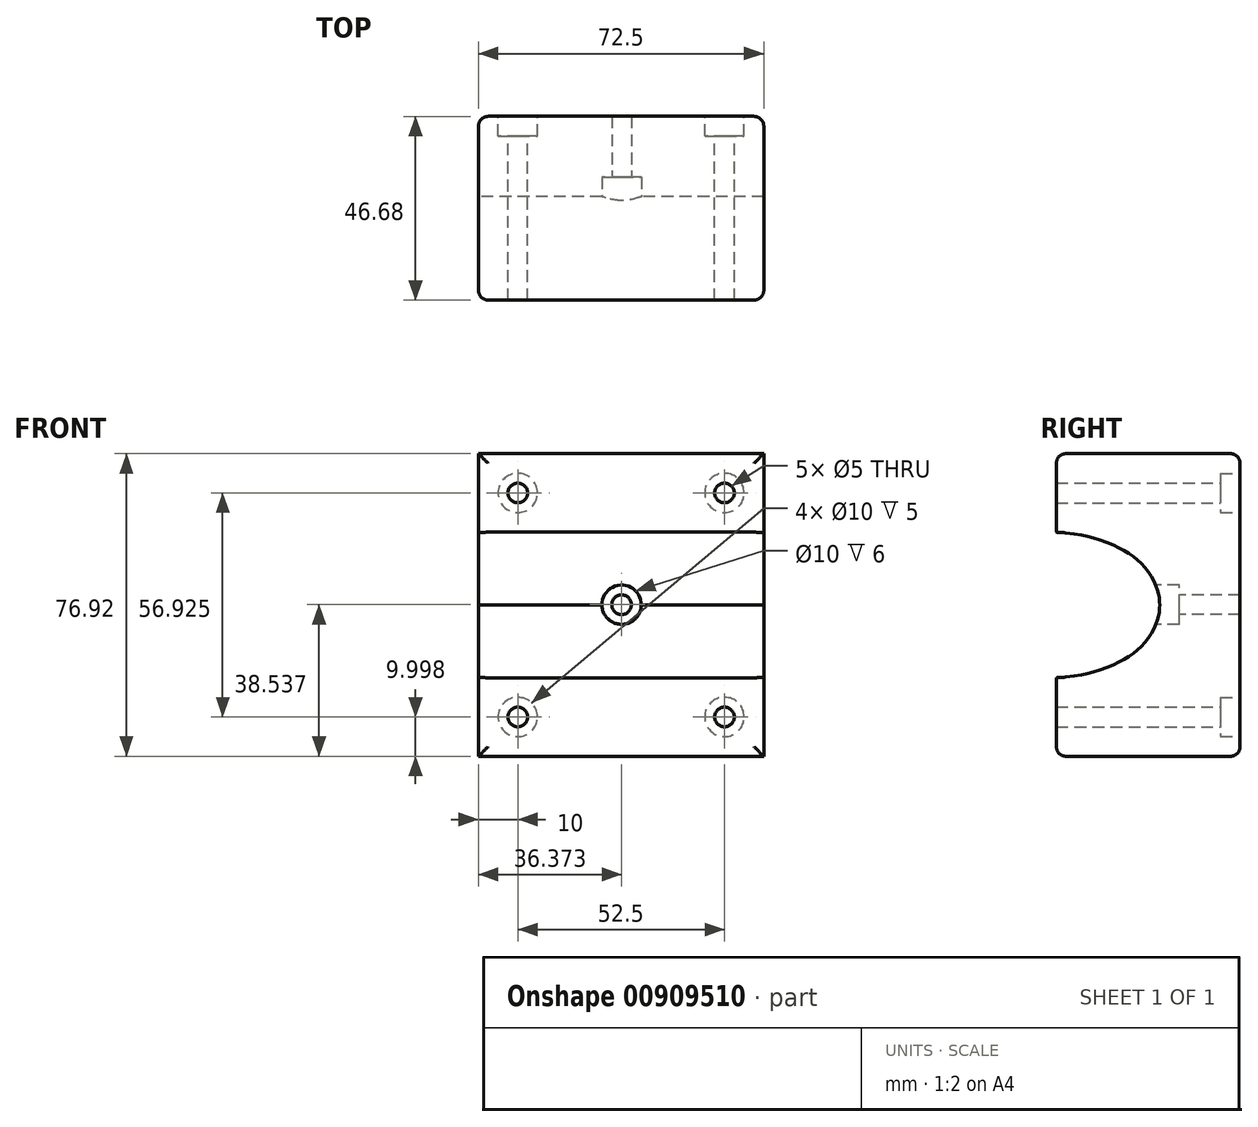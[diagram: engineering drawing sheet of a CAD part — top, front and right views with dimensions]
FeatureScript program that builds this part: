
annotation { "Feature Type Name" : "Feature", "Feature Type Description" : "" }
export const myFeature = defineFeature(function(context is Context, id is Id, definition is map)
    precondition{}
    {
        {
            var Q0;
            Q0=qCreatedBy(makeId("Right.planeOp"),FACE);
            var sketch = newSketch(context, id + "F0", { "sketchPlane" : qUnion([Q0])});
            skFitSpline(sketch, "E0.0", {"points": [v(-65.87, 0.89) * mm, v(-64.8, 1.67) * mm, v(-62.45, 3.19) * mm, v(-57.02, 6.06) * mm, v(-50.73, 8.67) * mm, v(-44.06, 10.98) * mm, v(-38.98, 12.54) * mm, v(-33.97, 13.9) * mm, v(-27.45, 15.46) * mm, v(-21.18, 16.65) * mm, v(-15.26, 17.5) * mm, v(-11.02, 18) * mm, v(-7, 18.34) * mm, v(-3.2, 18.55) * mm, v(0.4, 18.66) * mm, v(3.25, 18.68) * mm, v(5.47, 18.65) * mm, v(7.1, 18.62) * mm, v(8.7, 18.58) * mm, v(10.8, 18.5) * mm, v(13.41, 18.32) * mm, v(15.98, 18.01) * mm, v(18.01, 17.64) * mm, v(19.53, 17.3) * mm, v(21.04, 16.88) * mm, v(22.99, 16.25) * mm, v(24.85, 15.51) * mm, v(26.59, 14.7) * mm, v(27.81, 14.07) * mm, v(28.95, 13.42) * mm, v(30, 12.76) * mm, v(30.96, 12.06) * mm, v(31.85, 11.32) * mm, v(32.68, 10.52) * mm, v(33.46, 9.67) * mm, v(34.18, 8.74) * mm, v(34.86, 7.74) * mm, v(35.5, 6.7) * mm, v(36.05, 5.65) * mm, v(36.44, 4.76) * mm, v(36.7, 4.05) * mm, v(36.88, 3.52) * mm, v(37.01, 3) * mm, v(37.15, 2.32) * mm, v(37.25, 1.54) * mm, v(37.3, 0.7) * mm, v(37.3, 0.22) * mm, v(37.3, 0) * mm]});
            skLineSegment(sketch, "E1", {"start": v(11.06, 18.47) * mm, "end": v(11.06, 38.46) * mm});
            skLineSegment(sketch, "E2", {"start": v(11.06, 38.46) * mm, "end": v(57.74, 38.46) * mm});
            skFitSpline(sketch, "E3.MirrorCS", {"points": [v(-65.87, -0.89) * mm, v(-64.8, -1.67) * mm, v(-62.45, -3.19) * mm, v(-57.02, -6.06) * mm, v(-50.73, -8.67) * mm, v(-44.06, -10.98) * mm, v(-38.98, -12.54) * mm, v(-33.97, -13.9) * mm, v(-27.45, -15.46) * mm, v(-21.18, -16.65) * mm, v(-15.26, -17.5) * mm, v(-11.02, -18) * mm, v(-7, -18.34) * mm, v(-3.2, -18.55) * mm, v(0.4, -18.66) * mm, v(3.25, -18.68) * mm, v(5.47, -18.65) * mm, v(7.1, -18.62) * mm, v(8.7, -18.58) * mm, v(10.8, -18.5) * mm, v(13.41, -18.32) * mm, v(15.98, -18.01) * mm, v(18.01, -17.64) * mm, v(19.53, -17.3) * mm, v(21.04, -16.88) * mm, v(22.99, -16.25) * mm, v(24.85, -15.51) * mm, v(26.59, -14.7) * mm, v(27.81, -14.07) * mm, v(28.95, -13.42) * mm, v(30, -12.76) * mm, v(30.96, -12.06) * mm, v(31.85, -11.32) * mm, v(32.68, -10.52) * mm, v(33.46, -9.67) * mm, v(34.18, -8.74) * mm, v(34.86, -7.74) * mm, v(35.5, -6.7) * mm, v(36.05, -5.65) * mm, v(36.44, -4.76) * mm, v(36.7, -4.05) * mm, v(36.88, -3.52) * mm, v(37.01, -3) * mm, v(37.15, -2.32) * mm, v(37.25, -1.54) * mm, v(37.3, -0.7) * mm, v(37.3, -0.22) * mm, v(37.3, 0) * mm]});
            skLineSegment(sketch, "E4.MirrorCS", {"start": v(11.06, -38.46) * mm, "end": v(57.74, -38.46) * mm});
            skLineSegment(sketch, "E5.MirrorCS", {"start": v(11.06, -18.47) * mm, "end": v(11.06, -38.46) * mm});
            skLineSegment(sketch, "E6", {"start": v(57.74, 38.46) * mm, "end": v(57.74, -38.46) * mm});
            skSolve(sketch);
        }
        {
            var Q0;
            Q0=qSketchRegion(id+"F0",true);
            extrude(context, id + "F1", {"entities" : qUnion([Q0]), "depth" : 72.5 * mm, "offsetDistance" : 25 * mm});
        }
        {
            var Q0;
            Q0=makeQuery(id+"F1.opExtrude","SWEPT_FACE",FACE,{"disambiguationData":[OSD([sQuery(id+"F0.wireOp",EDGE,"E1")])]});
            var sketch = newSketch(context, id + "F2", { "sketchPlane" : qUnion([Q0])});
            skPoint(sketch, "E7", {"position": v(36.37, 0.08) * mm});
            skSolve(sketch);
        }
        {
            var Q0;
            Q0=sQuery(id+"F2.wireOp",VERTEX,"8a5668b4-76ee-41ec-8645-79288d4d8dce");
            var Q1;
            Q1=sQuery(id+"F2.wireOp",VERTEX,"E7");
            var Q2;
            Q2=makeQuery(id+"F1.opExtrude","SWEPT_BODY",BODY,{"disambiguationData":[OSD([sQuery(id+"F0.wireOp",EDGE,"E0.0"),sQuery(id+"F0.wireOp",EDGE,"E1"),sQuery(id+"F0.wireOp",EDGE,"E2"),sQuery(id+"F0.wireOp",EDGE,"E3.MirrorCS"),sQuery(id+"F0.wireOp",EDGE,"E4.MirrorCS"),sQuery(id+"F0.wireOp",EDGE,"E5.MirrorCS"),sQuery(id+"F0.wireOp",EDGE,"E6")])]});
            hole(context, id + "F3", {"style" : HoleStyle.C_BORE, "endStyle" : HoleEndStyle.THROUGH, "holeDiameter" : 5 * mm, "cBoreDiameter" : 10 * mm, "cBoreDepth" : 5 * mm, "majorDiameter" : 5 * mm, "isTappedThrough" : true, "tappedDepth" : 12 * mm, "tapClearance" : 3, "locations" : qUnion([Q0, Q1]), "scope" : qUnion([Q2])});
        }
        {
            var Q0;
            Q0=makeQuery(id+"F1.opExtrude","SWEPT_FACE",FACE,{"disambiguationData":[OSD([sQuery(id+"F0.wireOp",EDGE,"E6")])]});
            var sketch = newSketch(context, id + "F4", { "sketchPlane" : qUnion([Q0])});
            skSolve(sketch);
        }
        {
            var Q0;
            Q0=makeQuery(id+"F1.opExtrude","SWEPT_EDGE",EDGE,{"disambiguationData":[OSD([sQuery(id+"F0.wireOp",EDGE,"E4.MirrorCS"),sQuery(id+"F0.wireOp",EDGE,"E6")])]});
            var Q1;
            Q1=makeQuery(id+"F1.opExtrude","CAP_EDGE",EDGE,{"disambiguationData":[OSD([sQuery(id+"F0.wireOp",EDGE,"E6")])],"isStart":false});
            var Q2;
            Q2=makeQuery(id+"F1.opExtrude","SWEPT_EDGE",EDGE,{"disambiguationData":[OSD([sQuery(id+"F0.wireOp",EDGE,"E2"),sQuery(id+"F0.wireOp",EDGE,"E6")])]});
            var Q3;
            Q3=makeQuery(id+"F1.opExtrude","CAP_EDGE",EDGE,{"disambiguationData":[OSD([sQuery(id+"F0.wireOp",EDGE,"E6")])],"isStart":true});
            fillet(context, id + "F5", {"entities" : qUnion([Q0, Q1, Q2, Q3]), "radius" : 2.5 * mm, "tangentPropagation" : true, "allowEdgeOverflow" : false});
        }
        {
            var Q0;
            Q0=makeQuery(id+"F1.opExtrude","CAP_EDGE",EDGE,{"disambiguationData":[OSD([sQuery(id+"F0.wireOp",EDGE,"E1")])],"isStart":true});
            var Q1;
            Q1=makeQuery(id+"F1.opExtrude","SWEPT_EDGE",EDGE,{"disambiguationData":[OSD([sQuery(id+"F0.wireOp",EDGE,"E1"),sQuery(id+"F0.wireOp",EDGE,"E2")])]});
            var Q2;
            Q2=makeQuery(id+"F1.opExtrude","CAP_EDGE",EDGE,{"disambiguationData":[OSD([sQuery(id+"F0.wireOp",EDGE,"E1")])],"isStart":false});
            var Q3;
            Q3=makeQuery(id+"F1.opExtrude","CAP_EDGE",EDGE,{"disambiguationData":[OSD([sQuery(id+"F0.wireOp",EDGE,"E5.MirrorCS")])],"isStart":false});
            var Q4;
            Q4=makeQuery(id+"F1.opExtrude","SWEPT_EDGE",EDGE,{"disambiguationData":[OSD([sQuery(id+"F0.wireOp",EDGE,"E4.MirrorCS"),sQuery(id+"F0.wireOp",EDGE,"E5.MirrorCS")])]});
            var Q5;
            Q5=makeQuery(id+"F1.opExtrude","CAP_EDGE",EDGE,{"disambiguationData":[OSD([sQuery(id+"F0.wireOp",EDGE,"E5.MirrorCS")])],"isStart":true});
            fillet(context, id + "F6", {"entities" : qUnion([Q0, Q1, Q2, Q3, Q4, Q5]), "radius" : 2.5 * mm, "tangentPropagation" : true, "allowEdgeOverflow" : false});
        }
        {
            var Q0;
            {var subQ0=sQuery(id+"F0.wireOp",EDGE,"E6");Q0=makeQuery(id+"F4.imprint","IMPRINT",FACE,{"disambiguationData":[TD([[makeQuery(id+"F4.imprint","IMPRINT",EDGE,{"derivedFrom":makeQuery(id+"F1.opExtrude","CAP_EDGE",EDGE,{"disambiguationData":[OSD([subQ0])],"isStart":true})}),-1.0]])]});}
            var sketch = newSketch(context, id + "F7", { "sketchPlane" : qUnion([Q0])});
            skLineSegment(sketch, "E8", {"start": v(-87.6, 28.46) * mm, "end": v(9.67, 28.46) * mm});
            skLineSegment(sketch, "E9", {"start": v(-62.5, 42.62) * mm, "end": v(-62.5, -45.8) * mm});
            skPoint(sketch, "E10", {"position": v(-62.5, 28.46) * mm});
            skLineSegment(sketch, "E11", {"start": v(-10, 50.15) * mm, "end": v(-10, -46.25) * mm});
            skLineSegment(sketch, "E12", {"start": v(-91.74, -28.46) * mm, "end": v(11.22, -28.46) * mm});
            skPoint(sketch, "E13", {"position": v(-10, 28.46) * mm});
            skPoint(sketch, "E14", {"position": v(-62.5, -28.46) * mm});
            skPoint(sketch, "E15", {"position": v(-10, -28.46) * mm});
            skSolve(sketch);
        }
        {
            var Q0;
            Q0=sQuery(id+"F7.wireOp",VERTEX,"E10");
            var Q1;
            Q1=sQuery(id+"F7.wireOp",VERTEX,"E13");
            var Q2;
            Q2=sQuery(id+"F7.wireOp",VERTEX,"E14");
            var Q3;
            Q3=sQuery(id+"F7.wireOp",VERTEX,"E15");
            var Q4;
            Q4=makeQuery(id+"F1.opExtrude","SWEPT_BODY",BODY,{"disambiguationData":[OSD([sQuery(id+"F0.wireOp",EDGE,"E0.0"),sQuery(id+"F0.wireOp",EDGE,"E1"),sQuery(id+"F0.wireOp",EDGE,"E2"),sQuery(id+"F0.wireOp",EDGE,"E3.MirrorCS"),sQuery(id+"F0.wireOp",EDGE,"E4.MirrorCS"),sQuery(id+"F0.wireOp",EDGE,"E5.MirrorCS"),sQuery(id+"F0.wireOp",EDGE,"E6")])]});
            hole(context, id + "F8", {"style" : HoleStyle.C_BORE, "endStyle" : HoleEndStyle.THROUGH, "holeDiameter" : 5 * mm, "cBoreDiameter" : 10 * mm, "cBoreDepth" : 5 * mm, "majorDiameter" : 5 * mm, "isTappedThrough" : true, "tappedDepth" : 12 * mm, "tapClearance" : 3, "locations" : qUnion([Q0, Q1, Q2, Q3]), "scope" : qUnion([Q4])});
        }
    });
